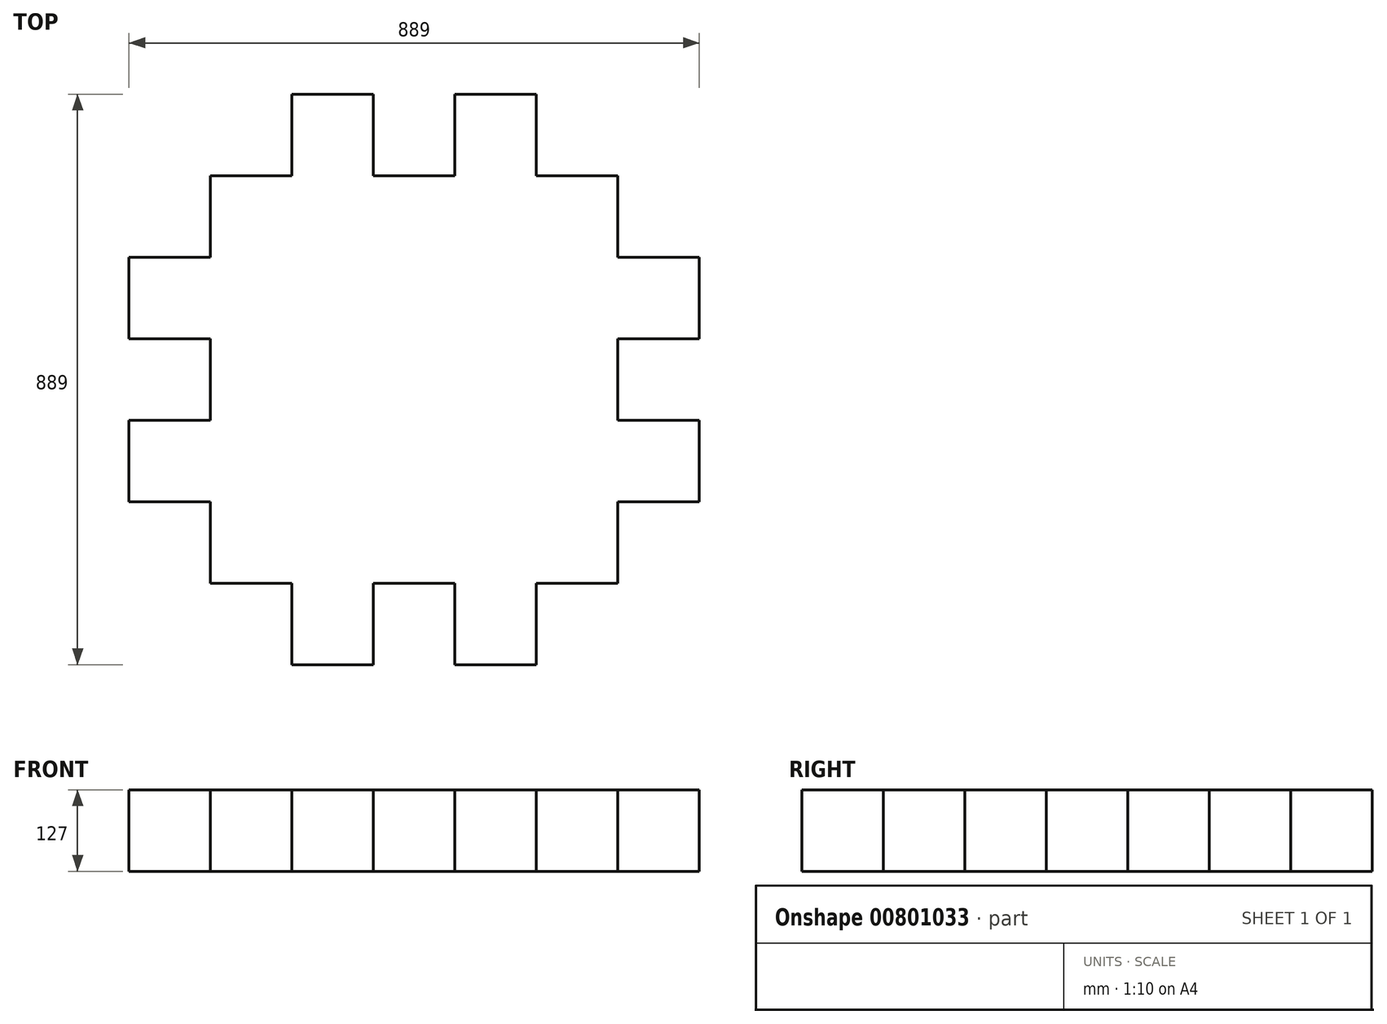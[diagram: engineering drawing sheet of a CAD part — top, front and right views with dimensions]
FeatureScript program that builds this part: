
annotation { "Feature Type Name" : "Feature", "Feature Type Description" : "" }
export const myFeature = defineFeature(function(context is Context, id is Id, definition is map)
    precondition{}
    {
        {
            var Q0;
            Q0=qCreatedBy(makeId("Top.planeOp"),FACE);
            var sketch = newSketch(context, id + "F0", { "sketchPlane" : qUnion([Q0])});
            skLineSegment(sketch, "E0.bottom", {"start": v(0, 0) * mm, "end": v(-635, 0) * mm});
            skLineSegment(sketch, "E0.top", {"start": v(0, 635) * mm, "end": v(-635, 635) * mm});
            skLineSegment(sketch, "E0.left", {"start": v(0, 0) * mm, "end": v(0, 635) * mm});
            skLineSegment(sketch, "E0.right", {"start": v(-635, 0) * mm, "end": v(-635, 635) * mm});
            skLineSegment(sketch, "E1.bottom", {"start": v(-635, 127) * mm, "end": v(-762, 127) * mm});
            skLineSegment(sketch, "E1.top", {"start": v(-635, 254) * mm, "end": v(-762, 254) * mm});
            skLineSegment(sketch, "E1.left", {"start": v(-635, 127) * mm, "end": v(-635, 254) * mm});
            skLineSegment(sketch, "E1.right", {"start": v(-762, 127) * mm, "end": v(-762, 254) * mm});
            skLineSegment(sketch, "E2.bottom", {"start": v(-635, 381) * mm, "end": v(-762, 381) * mm});
            skLineSegment(sketch, "E2.top", {"start": v(-635, 508) * mm, "end": v(-762, 508) * mm});
            skLineSegment(sketch, "E2.left", {"start": v(-635, 381) * mm, "end": v(-635, 508) * mm});
            skLineSegment(sketch, "E2.right", {"start": v(-762, 381) * mm, "end": v(-762, 508) * mm});
            skLineSegment(sketch, "E3.bottom", {"start": v(-508, 635) * mm, "end": v(-381, 635) * mm});
            skLineSegment(sketch, "E3.top", {"start": v(-508, 762) * mm, "end": v(-381, 762) * mm});
            skLineSegment(sketch, "E3.left", {"start": v(-508, 635) * mm, "end": v(-508, 762) * mm});
            skLineSegment(sketch, "E3.right", {"start": v(-381, 635) * mm, "end": v(-381, 762) * mm});
            skLineSegment(sketch, "E4.bottom", {"start": v(-254, 635) * mm, "end": v(-127, 635) * mm});
            skLineSegment(sketch, "E4.top", {"start": v(-254, 762) * mm, "end": v(-127, 762) * mm});
            skLineSegment(sketch, "E4.left", {"start": v(-254, 635) * mm, "end": v(-254, 762) * mm});
            skLineSegment(sketch, "E4.right", {"start": v(-127, 635) * mm, "end": v(-127, 762) * mm});
            skLineSegment(sketch, "E5.bottom", {"start": v(0, 508) * mm, "end": v(127, 508) * mm});
            skLineSegment(sketch, "E5.top", {"start": v(0, 381) * mm, "end": v(127, 381) * mm});
            skLineSegment(sketch, "E5.left", {"start": v(0, 508) * mm, "end": v(0, 381) * mm});
            skLineSegment(sketch, "E5.right", {"start": v(127, 508) * mm, "end": v(127, 381) * mm});
            skLineSegment(sketch, "E6.bottom", {"start": v(0, 127) * mm, "end": v(127, 127) * mm});
            skLineSegment(sketch, "E6.top", {"start": v(0, 254) * mm, "end": v(127, 254) * mm});
            skLineSegment(sketch, "E6.left", {"start": v(0, 127) * mm, "end": v(0, 254) * mm});
            skLineSegment(sketch, "E6.right", {"start": v(127, 127) * mm, "end": v(127, 254) * mm});
            skLineSegment(sketch, "E7.bottom", {"start": v(-127, 0) * mm, "end": v(-254, 0) * mm});
            skLineSegment(sketch, "E7.top", {"start": v(-127, -127) * mm, "end": v(-254, -127) * mm});
            skLineSegment(sketch, "E7.left", {"start": v(-127, 0) * mm, "end": v(-127, -127) * mm});
            skLineSegment(sketch, "E7.right", {"start": v(-254, 0) * mm, "end": v(-254, -127) * mm});
            skLineSegment(sketch, "E8.bottom", {"start": v(-381, 0) * mm, "end": v(-508, 0) * mm});
            skLineSegment(sketch, "E8.top", {"start": v(-381, -127) * mm, "end": v(-508, -127) * mm});
            skLineSegment(sketch, "E8.left", {"start": v(-381, 0) * mm, "end": v(-381, -127) * mm});
            skLineSegment(sketch, "E8.right", {"start": v(-508, 0) * mm, "end": v(-508, -127) * mm});
            skSolve(sketch);
        }
        {
            var Q0;
            Q0 = qSketchRegion(id + "F0", true);
            extrude(context, id + "F1", {"entities" : qUnion([Q0]), "depth" : 127 * mm, "offsetDistance" : 25.4 * mm});
        }
    });
